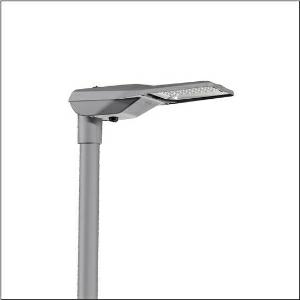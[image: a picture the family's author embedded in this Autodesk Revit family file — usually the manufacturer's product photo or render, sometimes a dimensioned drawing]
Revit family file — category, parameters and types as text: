
# Revit family: streetlight_sl_21_iq_mini___st0_8a_5xe2c31y08jb_7a77
name_source: partatom
category: Lighting Fixtures
units: mm (PartAtom-declared; Revit-internal decimal feet)

## family parameters
Cut with Voids When Loaded = No
Host = Face
Light Source = No
Part Type = Normal
Room Calculation Point = No
Round Connector Dimension = Use Diameter
Shared = No

## types (1)
- --- (1 x LED, 11210 lm, 72.5 W, 3000K)
    Apparent Load = 73 VA
    CIE Flux Codes = 41 75 97 100 100
    Color Rendering = 70
    Color Temperature = 3000K
    Default Elevation = 1800 mm
    Description = Streetlight SL 21 iQ mini, mast luminaire, primary light control with lens, of PMMA, primary optical cover: cover, of toughened safety glass, transparent, light distribution: ST0.8a, light emission: direct distribution, primary light characteristic: asymmetric, installation type: post-top, side-entry, LED, High Power LED, rated luminous flux: 11.210lm, luminous efficacy: 155lm/W, light colour: 730, colour temperature: 3000K, control gear: iQ-Street Remote, D4i with power reduction, control: pre-setting: logarithmic dimming characteristic, Street-Remote, Auto-Match, Temp-Guard, Lumen-Switch, Night-Set, Smart-Wire, Light-Fading, Desk-Remote (wireless, voltage-free reading and setting of iQ features in the workshop via application-optimized NFC function/RFID function), optimised constant luminous flux control (CLO 2.0), mains connection: 220..240V, AC, 50/60Hz, start of lifetime: 73W, end of service life: 76W, reduction: 33W, luminaire housing, of diecast aluminium, powder-coated, SITECO metallic grey (DB 702S), corrosivity category C5 high according to DIN EN ISO 12944, please order mast flange separately, inclination adjustable: 0°, 5°, 10°, 15°, sealing non-destructively replaceable, multi-level sealing system, length: 628mm, width: 235mm, height: 110mm, mast flange for spigot size: 42mm (side-entry): 5XC10008XM4, 60/48mm (side-entry/post-top): 5XC10108XM2, 76/60mm (side-entry/post-top): 5XC10108XM1, mounting height: 4..8m, Smart Interface below and above, protection rating (complete): IP66, insulation class (complete): insulation class II (safety insulation), certification: CE, ENEC, ENEC+, VDE, impact resistance: IK10, permissible operating ambient temperature for outdoor applications: -40..+50°C, standard-compliant lighting for roads and squares, packaging unit: 1 piece

Light Distribution: ST0.8a
    Height = 110 mm
    Lamp = 1 x LED
    Lamp Light Flux = 11210 lm
    Lamp Power = 72.5 W
    Lamp count = 1
    Length = 625 mm
    Luminous efficacy = 155 lm/W
    Manufacturer = Siteco
    ModVariant = No
    Model = 5XE2C31Y08JB
    Number of Poles = 1
    OnlyDefault = Yes
    Power Factor = 1
    Product Name = Streetlight SL 21 iQ mini | ST0.8a
    Product group = mast luminaire | pylon top
    ProductGroupID = 6100
    Protection Class = Protection class II
    Protection Degree = IP 66
    RLX_Detail_Level = 1
    RLX_Emergency_Light_Flux = 0 lm
    RLX_Emergency_Type = 0
    RLX_Emergency_Type_DB = No
    RlxData = <blob elided: 92541 chars, md5=42af42c3>
    Socket = socket
    Standby Power = 0 W
    System Light Flux = 11210 lm
    System Power = 73 W
    Type Comments = factory setting: luminous flux: 100 % | dim-lin: 254 | 755 mA
    Type Image = l_1003514.jpg
    URL = http://relux.com
    VarID = @adj_113355
    Voltage = 0 V
    Weight = 0.00 kg
    Width = 234 mm

## geometry (parser evidence)
native form markers: Blend x4, Sweep x13
no freeform markers — native parametric forms only
